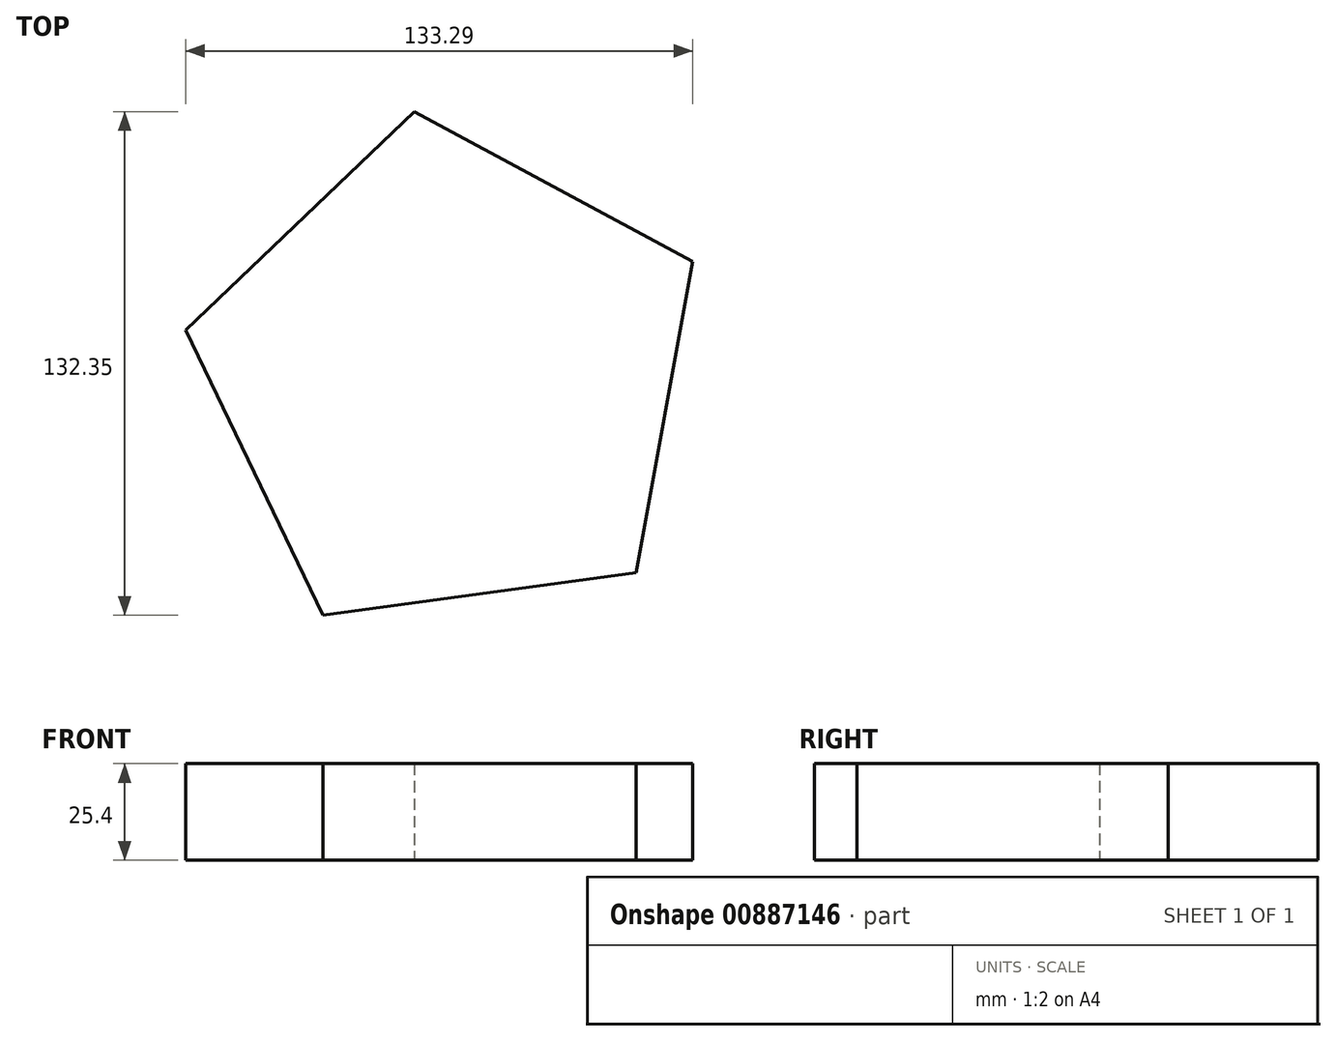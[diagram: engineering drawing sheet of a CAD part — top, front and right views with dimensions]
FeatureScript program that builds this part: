
annotation { "Feature Type Name" : "Feature", "Feature Type Description" : "" }
export const myFeature = defineFeature(function(context is Context, id is Id, definition is map)
    precondition{}
    {
        {
            var Q0;
            Q0=qCreatedBy(makeId("Top.planeOp"),FACE);
            var sketch = newSketch(context, id + "F0", { "sketchPlane" : qUnion([Q0])});
            skLineSegment(sketch, "E0", {"start": v(-51.35, 0) * mm, "end": v(-51.35, 30.42) * mm, "construction": true});
            skPoint(sketch, "E1", {"position": v(-51.35, 15.21) * mm});
            skCircle(sketch, "E2.cCircle", {"center": v(-51.35, 15.21) * mm, "radius": 57.2 * mm, "construction": true});
            skLineSegment(sketch, "E2.0", {"start": v(12.36, 45.89) * mm, "end": v(-2.5, -35.9) * mm});
            skLineSegment(sketch, "E2.1", {"start": v(-2.5, -35.9) * mm, "end": v(-84.87, -47.06) * mm});
            skLineSegment(sketch, "E2.2", {"start": v(-84.87, -47.06) * mm, "end": v(-120.93, 27.85) * mm});
            skLineSegment(sketch, "E2.3", {"start": v(-120.93, 27.85) * mm, "end": v(-60.84, 85.29) * mm});
            skLineSegment(sketch, "E2.4", {"start": v(-60.84, 85.29) * mm, "end": v(12.36, 45.89) * mm});
            skPoint(sketch, "E2.0.midPoint", {"position": v(4.94, 5) * mm});
            skSolve(sketch);
        }
        {
            var Q0;
            Q0=makeQuery(id+"F0.imprint","IMPRINT",FACE,{"disambiguationData":[TD([[makeQuery(id+"F0.imprint","IMPRINT",EDGE,{"derivedFrom":sQuery(id+"F0.wireOp",EDGE,"E2.0")}),-1.0]])]});
            extrude(context, id + "F1", {"entities" : qUnion([Q0]), "depth" : 25.4 * mm, "offsetDistance" : 25.4 * mm});
        }
    });
